# Revit family: CMP 250 V.V. EasyPlug
name_source: partatom
category: Equipement spécialisé
units: mm (PartAtom-declared; Revit-internal decimal feet)

## family parameters
Basée sur le plan de construction = Non
Conserver l'orientation des annotations = Non
Cote de connecteur circulaire = Utiliser le rayon
Couper avec des vides une fois chargée = Non
Numéro OmniClass = 23.40.40.14.14.11
Partagée = Non
Repère de localisation dans la pièce = Non
Titre OmniClass = Food Mixers
Toujours verticalement = Oui
Type d'élément = Normal

## types (6) — shared parameters
Apparent Power = 0 VA
Depth = 95 mm
Depth Electrique connexion = 48 mm  [stored 0.15748 ft]
Description = MIXERS PLONGEANTS GAMME COMPACTE CMP
Fabricant = ROBOT COUPE
Height = 619 mm
Height Electrique connexion = 607 mm
Modèle = CMP 250 V.V. EasyPlug
Phase = 1
URL = www.robot-coupe.com
Weight = 3.1 kg
Width = 201 mm  [stored 0.659449 ft]
water = Connector
zero-valued in all types: Cold water supply, Cold water supply height, Elévation par défaut, Used water, Waste water height

## per-type parameters (varying)
| type | Amps | Cycle | Speeds (Rpm) | Volts | Watts |
| CMP 250 V.V.   EasyPlug   230/50/1 | 1.4 A | 50 Hz | 2300 to 9600 | 230 V | 310 W |
| CMP 250 V.V.   EasyPlug   240/50/1 UK plug | 1.4 A | 50 Hz | 2300 to 9600 | 240 V | 310 W |
| CMP 250 V.V.   EasyPlug   120/60/1 | 2.6 A | 60 Hz | 2300 to 9600 | 120 V | 310 W |
| CMP 250 V.V   EasyPlug   220/60/1 | 1.3 A | 60 Hz | 2300 to 9600 | 220 V | 310 W |
| CMP 250 V.V.   EasyPlug   SAU   220/60/1 | 1.3 A | 60 Hz | 2300 to 9600 | 220 V | 310 W |
| CMP 250 V.V.   EasyPlug   120/60/1 USA | 2.3 A | 60 Hz | 5000 to 10000 | 120 V | 280 W |

note: [stored X ft] marks values corroborated as IEEE doubles in the binary element streams (Revit-internal decimal feet)

## geometry (parser evidence)
native form markers: Blend x86, Sweep x4
no freeform markers — native parametric forms only
